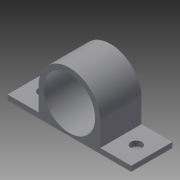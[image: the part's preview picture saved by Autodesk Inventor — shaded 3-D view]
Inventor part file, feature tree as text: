
AUTODESK INVENTOR PART (.ipt)
format: ipt  version: 2013 (Build 170138000, 138)  size: 128,512 bytes
history: native  units: in
note: dims shown in document units (in); Inventor stores cm internally (conversion verified against a paired STEP export)
features: extrude x2, sketch x2
ambient origin geometry x8: Origin, YZ Plane, XZ Plane, XY Plane, X Axis, Y Axis, Z Axis, Center Point
bodies: Solid1 (feature_tree)
feature tree (4):
  extrude  "Extrusion1"  Depth=1.5in
  extrude  "Extrusion2"  Depth=0.6875in
  sketch  "Sketch1"  dims[d0=1.5in d1=1.5in]
  sketch  "Sketch2"  dims[d2=0.125in d3=0.6875in d4=1.25in d5=0.125in d6=1.0in d7=0.0in d8=0.266in d11=1.0in d12=0.0in d13=0.375in d14=0.266in d15=0.375in]
